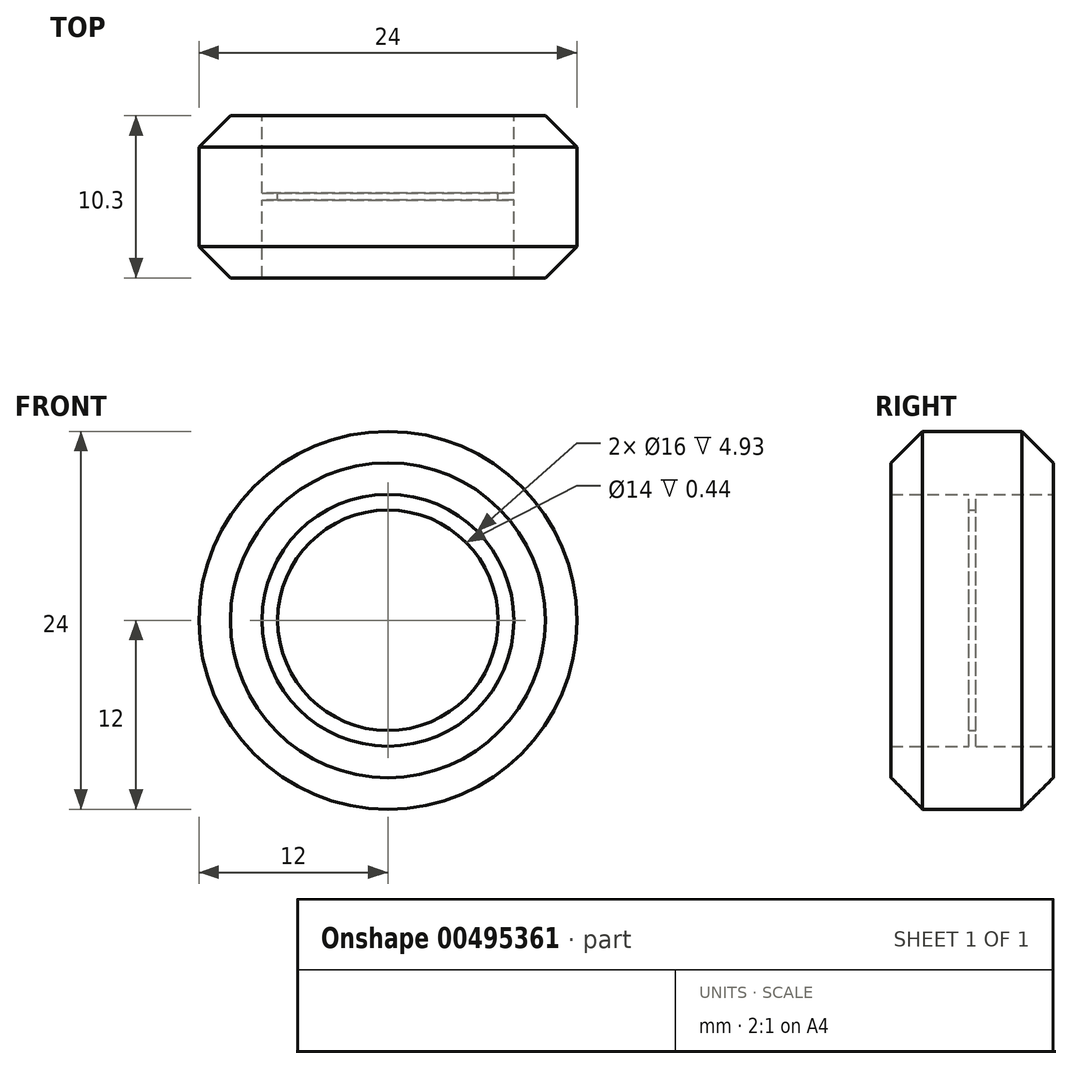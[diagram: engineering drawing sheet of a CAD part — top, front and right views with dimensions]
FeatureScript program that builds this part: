
annotation { "Feature Type Name" : "Feature", "Feature Type Description" : "" }
export const myFeature = defineFeature(function(context is Context, id is Id, definition is map)
    precondition{}
    {
        {
            var Q0;
            Q0=qCreatedBy(makeId("Front.planeOp"),FACE);
            var sketch = newSketch(context, id + "F0", { "sketchPlane" : qUnion([Q0])});
            skCircle(sketch, "E0", {"center": v(0, 0) * mm, "radius": 7 * mm});
            skCircle(sketch, "E1", {"center": v(0, 0) * mm, "radius": 8 * mm});
            skCircle(sketch, "E2", {"center": v(0, 0) * mm, "radius": 12 * mm});
            skSolve(sketch);
        }
        {
            var Q0;
            Q0=makeQuery(id+"F0.imprint","IMPRINT",FACE,{"disambiguationData":[TD([[makeQuery(id+"F0.imprint","IMPRINT",EDGE,{"derivedFrom":sQuery(id+"F0.wireOp",EDGE,"E1")}),-1.0]])]});
            extrude(context, id + "F1", {"entities" : qUnion([Q0]), "depth" : 5.15 * mm});
        }
        {
            var Q0;
            Q0=makeQuery(id+"F0.imprint","IMPRINT",FACE,{"disambiguationData":[TD([[makeQuery(id+"F0.imprint","IMPRINT",EDGE,{"derivedFrom":sQuery(id+"F0.wireOp",EDGE,"E1")}),-1.0]])]});
            extrude(context, id + "F2", {"entities" : qUnion([Q0]), "operationType" : NewBodyOperationType.ADD, "oppositeDirection" : true, "depth" : 5.15 * mm});
        }
        {
            var Q0;
            Q0=makeQuery(id+"F0.imprint","IMPRINT",FACE,{"disambiguationData":[TD([[makeQuery(id+"F0.imprint","IMPRINT",EDGE,{"derivedFrom":sQuery(id+"F0.wireOp",EDGE,"E0")}),-1.0]])]});
            extrude(context, id + "F3", {"entities" : qUnion([Q0]), "operationType" : NewBodyOperationType.ADD, "depth" : .22 * mm});
        }
        {
            var Q0;
            Q0=makeQuery(id+"F0.imprint","IMPRINT",FACE,{"disambiguationData":[TD([[makeQuery(id+"F0.imprint","IMPRINT",EDGE,{"derivedFrom":sQuery(id+"F0.wireOp",EDGE,"E0")}),-1.0]])]});
            extrude(context, id + "F4", {"entities" : qUnion([Q0]), "operationType" : NewBodyOperationType.ADD, "oppositeDirection" : true, "depth" : .22 * mm});
        }
        {
            var Q0;
            Q0=makeQuery(id+"F1.opExtrude","CAP_EDGE",EDGE,{"disambiguationData":[OSD([sQuery(id+"F0.wireOp",EDGE,"E2")])],"isStart":false});
            var Q1;
            Q1=makeQuery(id+"F2.opExtrude","CAP_EDGE",EDGE,{"disambiguationData":[OSD([sQuery(id+"F0.wireOp",EDGE,"E2")])],"isStart":false});
            chamfer(context, id + "F5", {"entities" : qUnion([Q0, Q1]), "width" : 2 * mm, "tangentPropagation" : true});
        }
    });
